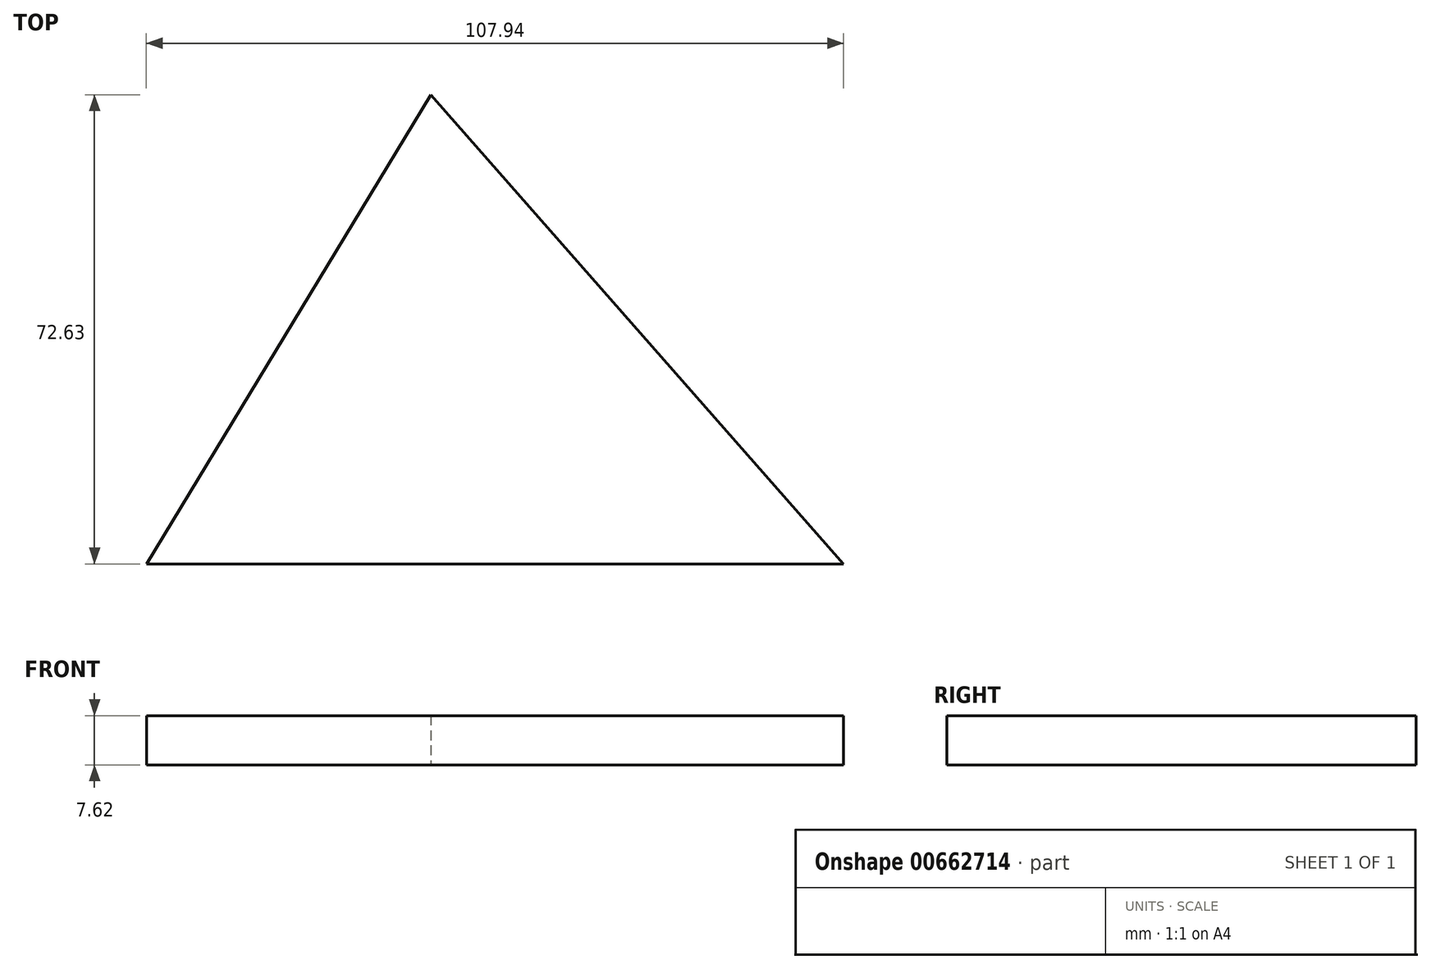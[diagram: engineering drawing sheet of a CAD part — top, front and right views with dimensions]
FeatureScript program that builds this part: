
annotation { "Feature Type Name" : "Feature", "Feature Type Description" : "" }
export const myFeature = defineFeature(function(context is Context, id is Id, definition is map)
    precondition{}
    {
        {
            var Q0;
            Q0=qCreatedBy(makeId("Top.planeOp"),FACE);
            var sketch = newSketch(context, id + "F0", { "sketchPlane" : qUnion([Q0])});
            skLineSegment(sketch, "E0", {"start": v(-15.03, 72.63) * mm, "end": v(-59.09, 0) * mm});
            skLineSegment(sketch, "E1", {"start": v(-59.09, 0) * mm, "end": v(48.85, 0) * mm});
            skLineSegment(sketch, "E2", {"start": v(48.85, 0) * mm, "end": v(-15.03, 72.63) * mm});
            skSolve(sketch);
        }
        {
            var Q0;
            Q0=makeQuery(id+"F0.imprint","IMPRINT",FACE,{"disambiguationData":[TD([[makeQuery(id+"F0.imprint","IMPRINT",EDGE,{"derivedFrom":sQuery(id+"F0.wireOp",EDGE,"E0")}),1.0]])]});
            var sketch = newSketch(context, id + "F1", { "sketchPlane" : qUnion([Q0])});
            skSolve(sketch);
        }
        {
            var Q0;
            Q0=makeQuery(id+"F1.imprint","IMPRINT",FACE,{"disambiguationData":[TD([[makeQuery(id+"F1.imprint","IMPRINT",EDGE,{"derivedFrom":makeQuery(id+"F0.imprint","IMPRINT",EDGE,{"derivedFrom":sQuery(id+"F0.wireOp",EDGE,"E0")})}),1.0]])]});
            extrude(context, id + "F2", {"entities" : qUnion([Q0]), "depth" : 7.62 * mm, "offsetDistance" : 25.4 * mm});
        }
    });
